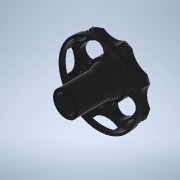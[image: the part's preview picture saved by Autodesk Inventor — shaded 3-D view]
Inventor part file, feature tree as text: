
AUTODESK INVENTOR PART (.ipt)
format: ipt  version: 2022 (Build 260153000, 153)  size: 305,152 bytes
history: native  units: in
note: dims shown in document units (in); Inventor stores cm internally (conversion verified against a paired STEP export)
features: sketch x2, revolve x1, extrude x1
ambient origin geometry x8: Origin, YZ Plane, XZ Plane, XY Plane, X Axis, Y Axis, Z Axis, Center Point
bodies: Solid1 (feature_tree)
feature tree (4):
  revolve  "Revolution1"  [1 undecoded]
  extrude  "Extrusion1"  Depth=0.0787in
  sketch  "Sketch1"  dims[d0=0.8366in d1=0.2559in]
  sketch  "Sketch2"  dims[d2=0.7874in d3=0.0787in d4=0.063in d5=0.0394in d6=0.0394in d7=0.0315in d8=0.0197in d9=0.0492in d10=0.1476in d11=0.315in d12=0.2756in d13=0.1969in d14=0.1575in d15=0.1575in d16=0.7087in d17=0.1969in d18=0.1575in d19=0.2657in d20=90.0deg d21=0.9843in d22=0.1181in d23=0.2756in d24=0.1718in d25=0.0197in d26=0.2749in d27=0.7874in d28=1.378in d29=1.5748in d31=360.0deg d33=3.1496in d35=360.0deg d37=0.2362in d38=0.0in]
note: 1 required parameter value undecoded (feature->parameter linkage not recoverable at this tier; creation-order binding heuristic only, values carry confidence <= 0.55)
